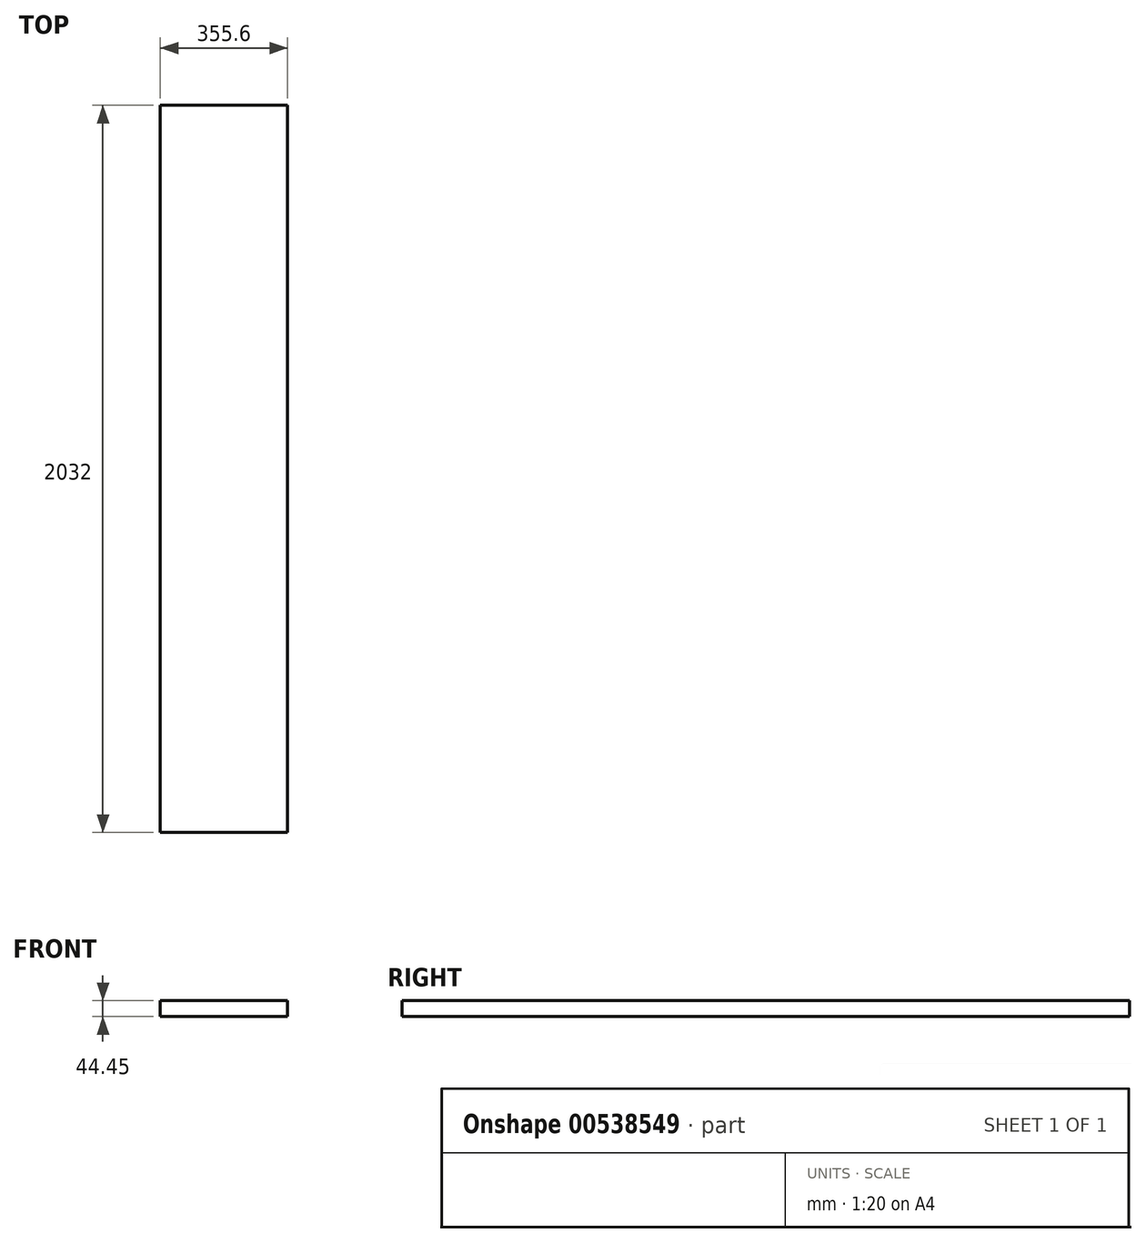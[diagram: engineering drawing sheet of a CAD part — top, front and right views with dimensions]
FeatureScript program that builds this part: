
annotation { "Feature Type Name" : "Feature", "Feature Type Description" : "" }
export const myFeature = defineFeature(function(context is Context, id is Id, definition is map)
    precondition{}
    {
        {
            var Q0;
            Q0=qCreatedBy(makeId("Top.planeOp"),FACE);
            var sketch = newSketch(context, id + "F0", { "sketchPlane" : qUnion([Q0])});
            skLineSegment(sketch, "E0.bottom", {"start": v(-177.8, 1016) * mm, "end": v(177.8, 1016) * mm});
            skLineSegment(sketch, "E0.top", {"start": v(-177.8, -1016) * mm, "end": v(177.8, -1016) * mm});
            skLineSegment(sketch, "E0.left", {"start": v(-177.8, 1016) * mm, "end": v(-177.8, -1016) * mm});
            skLineSegment(sketch, "E0.right", {"start": v(177.8, 1016) * mm, "end": v(177.8, -1016) * mm});
            skPoint(sketch, "E0.middle", {"position": v(0, 0) * mm});
            skSolve(sketch);
        }
        {
            var Q0;
            Q0=makeQuery(id+"F0.imprint","IMPRINT",FACE,{"disambiguationData":[TD([[makeQuery(id+"F0.imprint","IMPRINT",EDGE,{"derivedFrom":sQuery(id+"F0.wireOp",EDGE,"E0.bottom")}),-1.0]])]});
            extrude(context, id + "F1", {"entities" : qUnion([Q0]), "depth" : 44.45 * mm, "offsetDistance" : 25.4 * mm});
        }
    });
